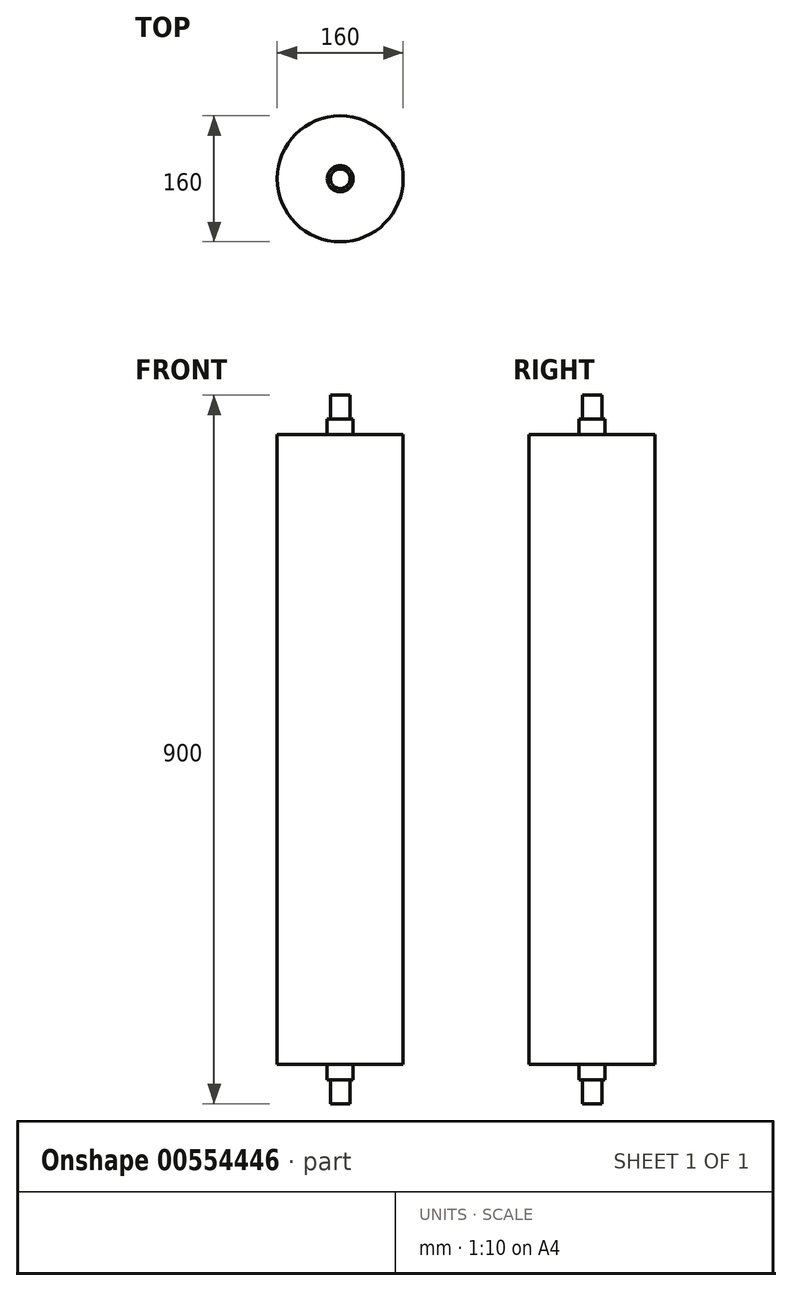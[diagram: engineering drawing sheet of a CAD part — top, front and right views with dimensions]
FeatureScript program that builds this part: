
annotation { "Feature Type Name" : "Feature", "Feature Type Description" : "" }
export const myFeature = defineFeature(function(context is Context, id is Id, definition is map)
    precondition{}
    {
        {
            var Q0;
            Q0=qCreatedBy(makeId("Front.planeOp"),FACE);
            var sketch = newSketch(context, id + "F0", { "sketchPlane" : qUnion([Q0])});
            skLineSegment(sketch, "E0", {"start": v(-100, 450) * mm, "end": v(-112.5, 450) * mm});
            skLineSegment(sketch, "E1", {"start": v(-112.5, 450) * mm, "end": v(-112.5, 420) * mm});
            skLineSegment(sketch, "E2", {"start": v(-112.5, 420) * mm, "end": v(-116.5, 420) * mm});
            skLineSegment(sketch, "E3", {"start": v(-116.5, 420) * mm, "end": v(-116.5, 400) * mm});
            skLineSegment(sketch, "E4", {"start": v(-116.5, 400) * mm, "end": v(-180, 400) * mm});
            skLineSegment(sketch, "E5", {"start": v(-180, 400) * mm, "end": v(-180, -400) * mm});
            skLineSegment(sketch, "E6", {"start": v(-180, -400) * mm, "end": v(-116.5, -400) * mm});
            skLineSegment(sketch, "E7", {"start": v(-116.5, -400) * mm, "end": v(-116.5, -420) * mm});
            skLineSegment(sketch, "E8", {"start": v(-116.5, -420) * mm, "end": v(-112.5, -420) * mm});
            skLineSegment(sketch, "E9", {"start": v(-112.5, -420) * mm, "end": v(-112.5, -450) * mm});
            skLineSegment(sketch, "E10", {"start": v(-112.5, -450) * mm, "end": v(-100, -450) * mm});
            skLineSegment(sketch, "E11", {"start": v(-100, -450) * mm, "end": v(-100, 450) * mm});
            skLineSegment(sketch, "E12", {"start": v(-189.9, 0) * mm, "end": v(13.05, 0) * mm, "construction": true});
            skLineSegment(sketch, "E13", {"start": v(-100, 521.94) * mm, "end": v(-100, -509.74) * mm, "construction": true});
            skSolve(sketch);
        }
        {
            var Q0;
            Q0=makeQuery(id+"F0.imprint","IMPRINT",FACE,{"disambiguationData":[TD([[makeQuery(id+"F0.imprint","IMPRINT",EDGE,{"derivedFrom":sQuery(id+"F0.wireOp",EDGE,"E0")}),1.0]])]});
            var Q1;
            Q1=sQuery(id+"F0.wireOp",EDGE,"E13");
            revolve(context, id + "F1", {"entities" : qUnion([Q0]), "axis" : qUnion([Q1]), "revolveType" : RevolveType.FULL});
        }
    });
